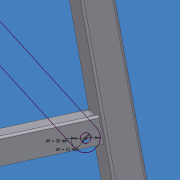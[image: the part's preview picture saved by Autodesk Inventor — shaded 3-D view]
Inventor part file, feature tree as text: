
AUTODESK INVENTOR PART (.ipt)
format: ipt  version: 2015 (Build 190159000, 159)  size: 73,728 bytes
history: native  units: mm
features: reference x2, extrude x1, sketch x1
ambient origin geometry x8: Origin, YZ Plane, XZ Plane, XY Plane, X Axis, Y Axis, Z Axis, Center Point
bodies: Solid1 (feature_tree)
feature tree (4):
  extrude  "Extrusion2"  Depth=6.0mm
  sketch  "Sketch1"  dims[d2=30.0mm d3=11.0mm d4=11.0mm d5=30.0mm d6=6.0mm d7=0.0mm]
  reference  "Reference1"
  reference  "Reference2"
